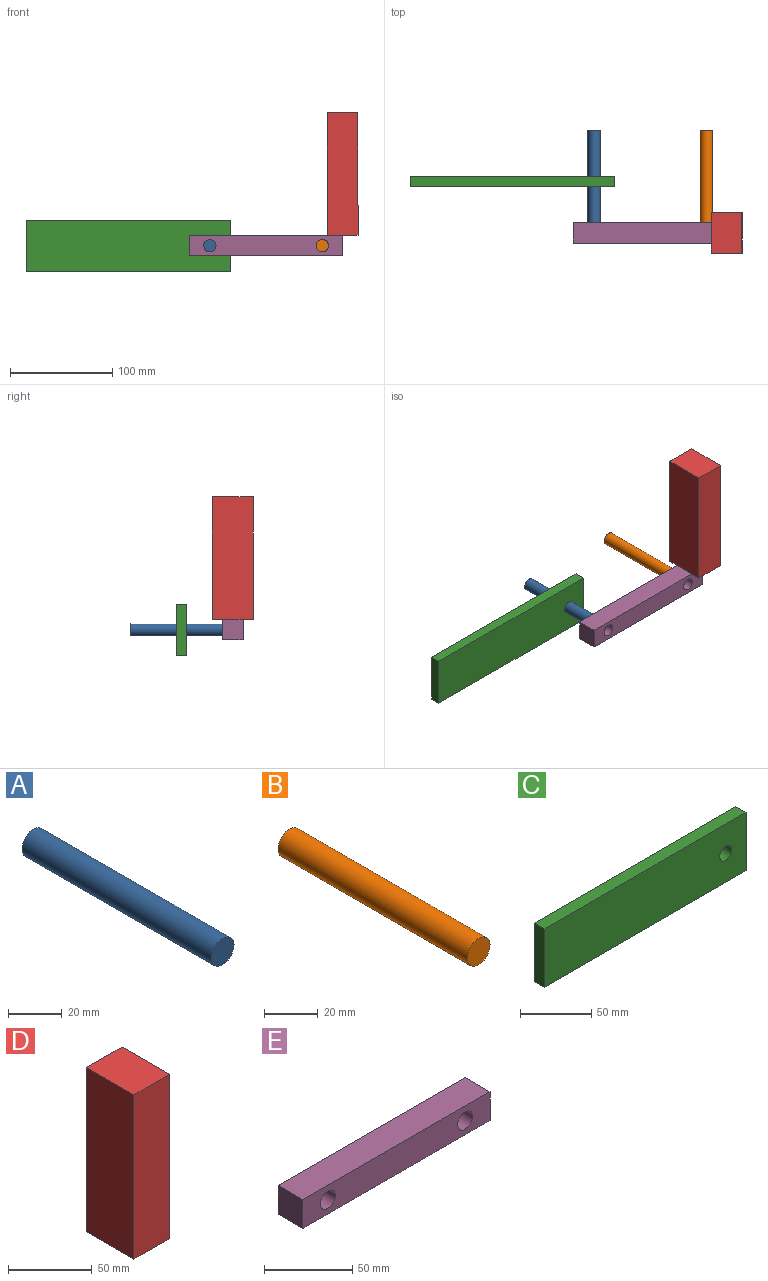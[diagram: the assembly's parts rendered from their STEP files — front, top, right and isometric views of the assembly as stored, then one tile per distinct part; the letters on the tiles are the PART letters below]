
ASSEMBLY  parts=5 mates=4
PART A: 3 faces, bbox 12x100x12 mm
  f0: cylinder r=6mm len=100mm, axis (0,1,0), area 3769.9mm2, adj f1,f2
  f1: plane 12x12mm, normal (0,-1,0), area 113.1mm2, adj f0
  f2: plane 12x12mm, normal (0,1,0), area 113.1mm2, adj f0
PART B: 3 faces, bbox 12x100x12 mm
  f0: cylinder r=6mm len=100mm, axis (0,1,0), area 3769.9mm2, adj f1,f2
  f1: plane 12x12mm, normal (0,-1,0), area 113.1mm2, adj f0
  f2: plane 12x12mm, normal (0,1,0), area 113.1mm2, adj f0
PART C: 7 faces, bbox 200x10x50 mm
  f0: plane 50x10mm, normal (1,0,0), area 500mm2, adj f1,f3,f5,f6
  f1: plane 200x10mm, normal (0,0,1), area 2000mm2, adj f0,f2,f5,f6
  f2: plane 50x10mm, normal (-1,0,0), area 500mm2, adj f1,f3,f5,f6
  f3: plane 200x10mm, normal (0,0,-1), area 2000mm2, adj f0,f2,f5,f6
  f4: cylinder r=6mm len=12mm, axis (0,1,0), area 377mm2, adj f5,f6
  f5: plane 200x50mm, normal (0,-1,0), area 9886.9mm2, adj f0,f1,f2,f3,f4
  f6: plane 200x50mm, normal (0,1,0), area 9886.9mm2, adj f0,f1,f2,f3,f4
PART D: 6 faces, bbox 30x40x120 mm
  f0: plane 120x40mm, normal (-1,0,0), area 4800mm2, adj f1,f3,f4,f5
  f1: plane 40x30mm, normal (0,0,-1), area 1200mm2, adj f0,f2,f4,f5
  f2: plane 120x40mm, normal (1,0,0), area 4800mm2, adj f1,f3,f4,f5
  f3: plane 40x30mm, normal (0,0,1), area 1200mm2, adj f0,f2,f4,f5
  f4: plane 120x30mm, normal (0,-1,0), area 3600mm2, adj f0,f1,f2,f3
  f5: plane 120x30mm, normal (0,1,0), area 3600mm2, adj f0,f1,f2,f3
PART E: 8 faces, bbox 150x20x20 mm
  f0: plane 150x20mm, normal (0,0,1), area 3000mm2, adj f1,f4,f6,f7
  f1: plane 20x20mm, normal (-1,0,0), area 400mm2, adj f0,f2,f6,f7
  f2: plane 150x20mm, normal (0,0,-1), area 3000mm2, adj f1,f4,f6,f7
  f3: cylinder r=6mm len=20mm, axis (0,1,0), area 754mm2, adj f6,f7
  f4: plane 20x20mm, normal (1,0,0), area 400mm2, adj f0,f2,f6,f7
  f5: cylinder r=6mm len=20mm, axis (0,1,0), area 754mm2, adj f6,f7
  f6: plane 150x20mm, normal (0,-1,0), area 2773.8mm2, adj f0,f1,f2,f3,f4,f5
  f7: plane 150x20mm, normal (0,1,0), area 2773.8mm2, adj f0,f1,f2,f3,f4,f5
PLACE A at identity
PLACE B at identity fixed
PLACE C at identity
PLACE D rot(axis=(0.15,-0.98,-0.12),0deg) t=(20,-20,0)mm
PLACE E rot(axis=(-0.02,0.99,0.1),0deg) t=(0,-20,0)mm
MATE revolute A.f0 <-> E.f3  axis (0,-1,0) through (0,-50,0)mm
MATE revolute C.f4 <-> A.f0  axis (0,1,0) through (0,0,0)mm
MATE revolute E.f5 <-> B.f0  axis (0,1,0) through (110,-50,0)mm
MATE fastened D.f1 <-> E.f0  axis (0,0,-1) through (130,-50,10)mm
